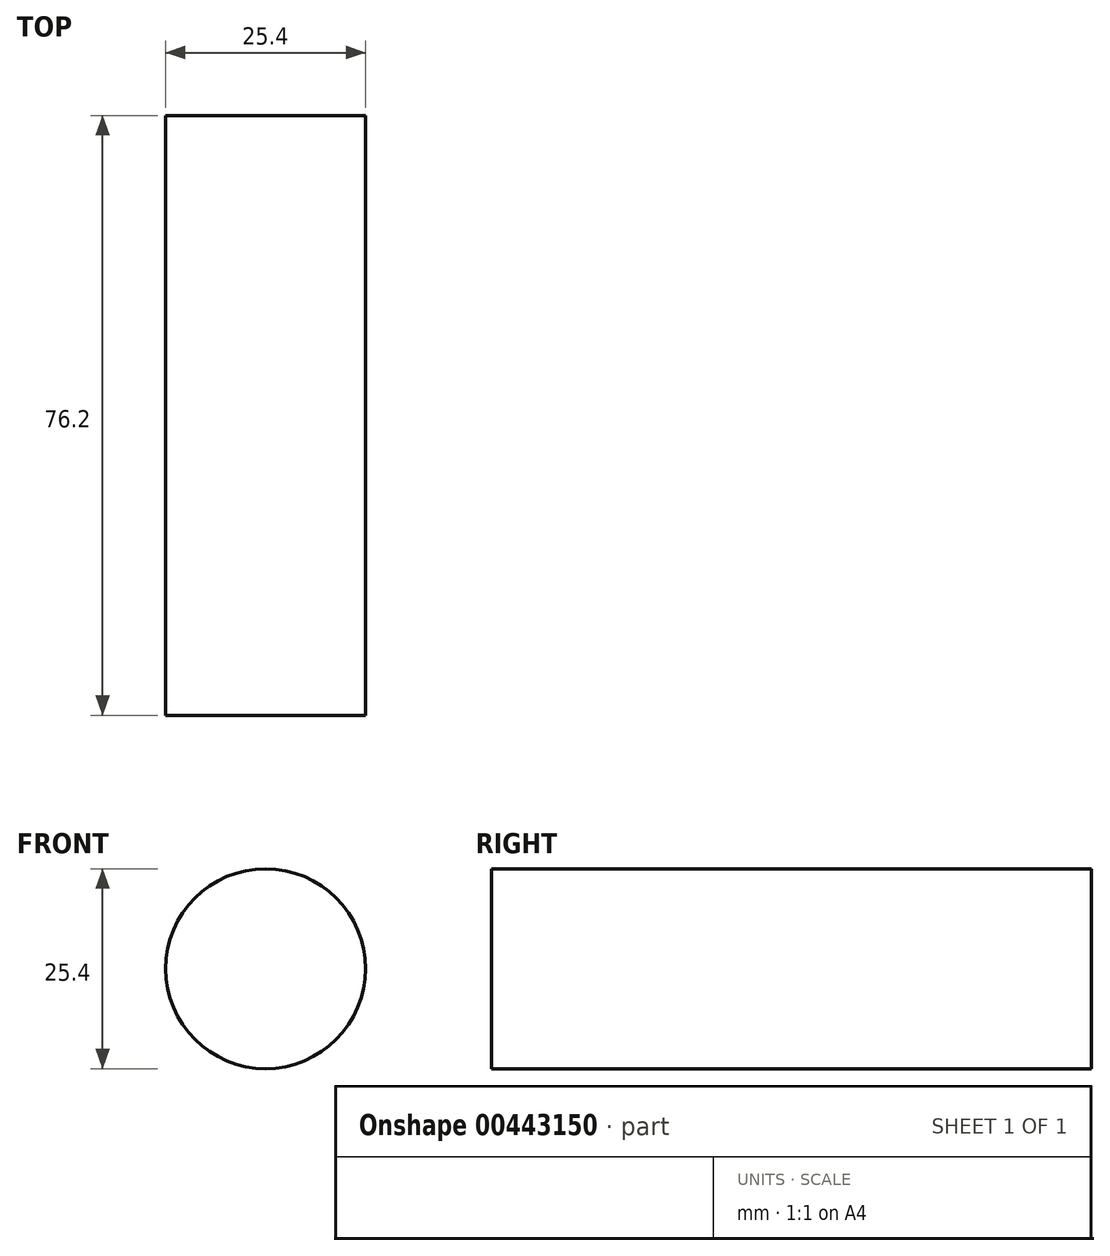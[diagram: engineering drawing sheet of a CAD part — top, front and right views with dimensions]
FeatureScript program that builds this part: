
annotation { "Feature Type Name" : "Feature", "Feature Type Description" : "" }
export const myFeature = defineFeature(function(context is Context, id is Id, definition is map)
    precondition{}
    {
        {
            var Q0;
            Q0=qCreatedBy(makeId("Front.planeOp"),FACE);
            var sketch = newSketch(context, id + "F0", { "sketchPlane" : qUnion([Q0])});
            skCircle(sketch, "E0", {"center": v(-48.64, 36.84) * mm, "radius": 12.7 * mm});
            skSolve(sketch);
        }
        {
            var Q0;
            Q0=makeQuery(id+"F0.imprint","IMPRINT",FACE,{"disambiguationData":[TD([[makeQuery(id+"F0.imprint","IMPRINT",EDGE,{"derivedFrom":sQuery(id+"F0.wireOp",EDGE,"E0")}),1.0]])]});
            extrude(context, id + "F1", {"entities" : qUnion([Q0]), "depth" : 76.2 * mm, "offsetDistance" : 25.4 * mm});
        }
    });
